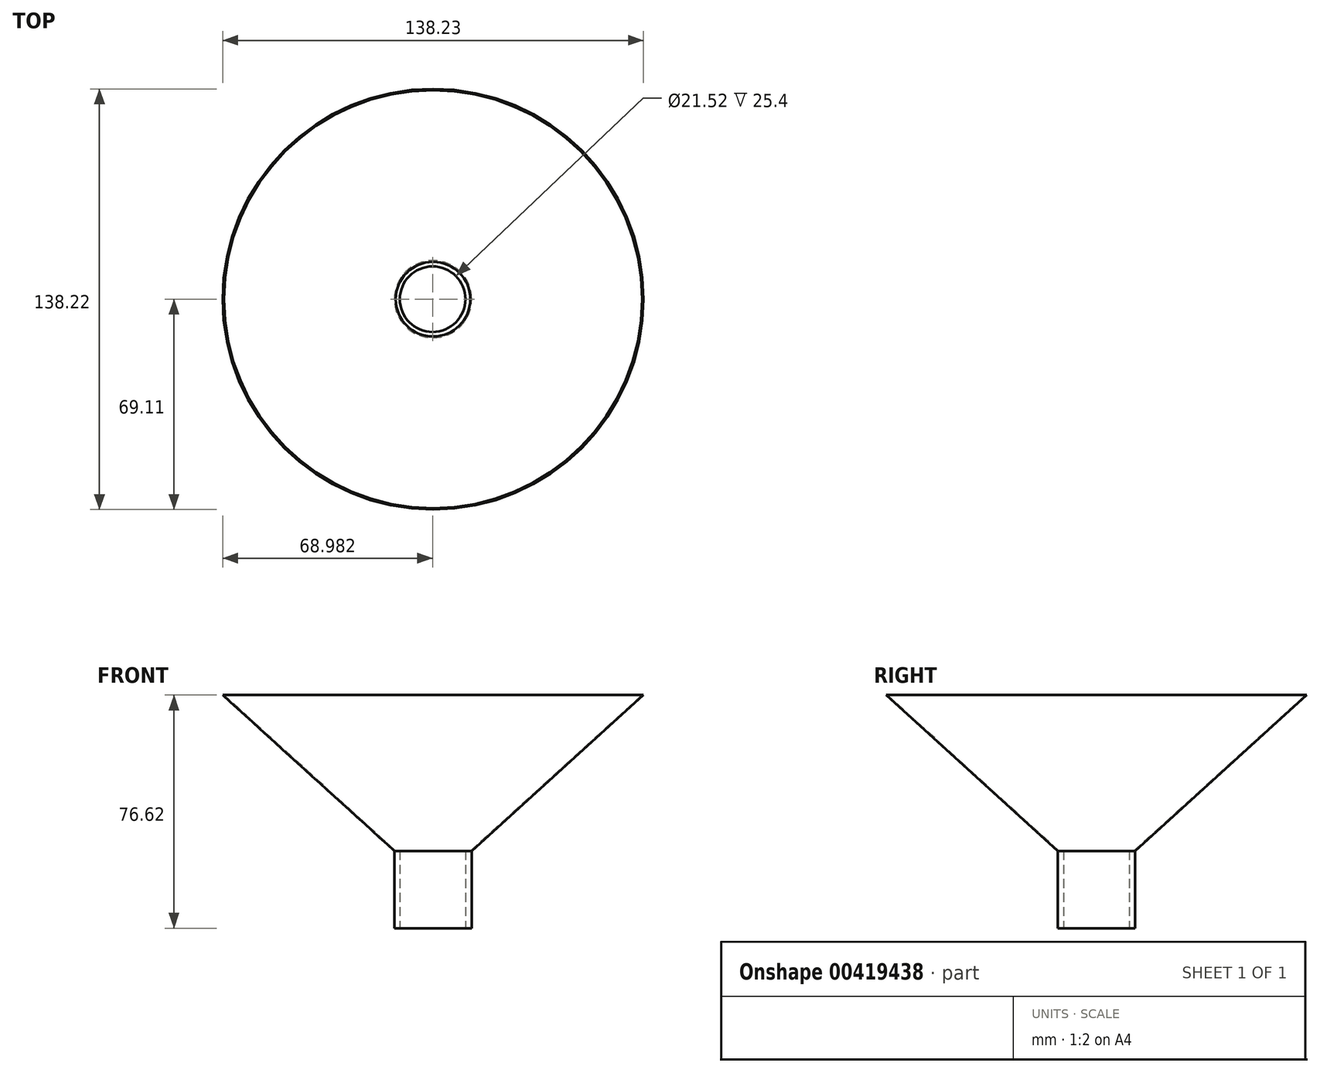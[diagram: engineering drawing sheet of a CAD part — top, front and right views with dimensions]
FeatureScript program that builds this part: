
annotation { "Feature Type Name" : "Feature", "Feature Type Description" : "" }
export const myFeature = defineFeature(function(context is Context, id is Id, definition is map)
    precondition{}
    {
        {
            var Q0;
            Q0=qCreatedBy(makeId("Front.planeOp"),FACE);
            var sketch = newSketch(context, id + "F0", { "sketchPlane" : qUnion([Q0])});
            skLineSegment(sketch, "E0", {"start": v(64.15, 38.6) * mm, "end": v(7.74, -12.63) * mm});
            skLineSegment(sketch, "E1", {"start": v(7.74, -38.03) * mm, "end": v(7.74, -12.63) * mm});
            skLineSegment(sketch, "E2", {"start": v(7.74, -38.03) * mm, "end": v(-4.96, -38.03) * mm});
            skLineSegment(sketch, "E3", {"start": v(-4.96, -38.03) * mm, "end": v(-4.96, -12.63) * mm});
            skLineSegment(sketch, "E4", {"start": v(-4.96, -12.63) * mm, "end": v(7.3, -12.63) * mm});
            skLineSegment(sketch, "E5", {"start": v(7.3, -12.63) * mm, "end": v(63.7, 38.6) * mm});
            skLineSegment(sketch, "E6", {"start": v(63.7, 38.6) * mm, "end": v(64.15, 38.6) * mm});
            skSolve(sketch);
        }
        {
            var Q0;
            Q0 = qSketchRegion(id + "F0", true);
            var Q1;
            Q1=sQuery(id+"F0.wireOp",EDGE,"E3");
            revolve(context, id + "F1", {"entities" : qUnion([Q0]), "axis" : qUnion([Q1]), "revolveType" : RevolveType.FULL});
        }
        {
            var Q0;
            Q0=makeQuery(id+"F1.opRevolve","SWEPT_FACE",FACE,{"disambiguationData":[OSD([sQuery(id+"F0.wireOp",EDGE,"E2")])]});
            var sketch = newSketch(context, id + "F2", { "sketchPlane" : qUnion([Q0])});
            skSolve(sketch);
        }
        {
            var Q0;
            Q0=makeQuery(id+"F2.imprint","IMPRINT",FACE,{"disambiguationData":[TD([[makeQuery(id+"F2.imprint","IMPRINT",EDGE,{"derivedFrom":makeQuery(id+"F1.opRevolve","SWEPT_EDGE",EDGE,{"disambiguationData":[OSD([sQuery(id+"F0.wireOp",EDGE,"E1"),sQuery(id+"F0.wireOp",EDGE,"E2")])]})}),1.0]])]});
            var sketch = newSketch(context, id + "F3", { "sketchPlane" : qUnion([Q0])});
            skCircle(sketch, "E7", {"center": v(-5.1, 0) * mm, "radius": 10.76 * mm});
            skSolve(sketch);
        }
        {
            var Q0;
            Q0 = qSketchRegion(id + "F3", true);
            extrude(context, id + "F4", {"entities" : qUnion([Q0]), "operationType" : NewBodyOperationType.REMOVE, "oppositeDirection" : true, "depth" : 25.4 * mm});
        }
    });
